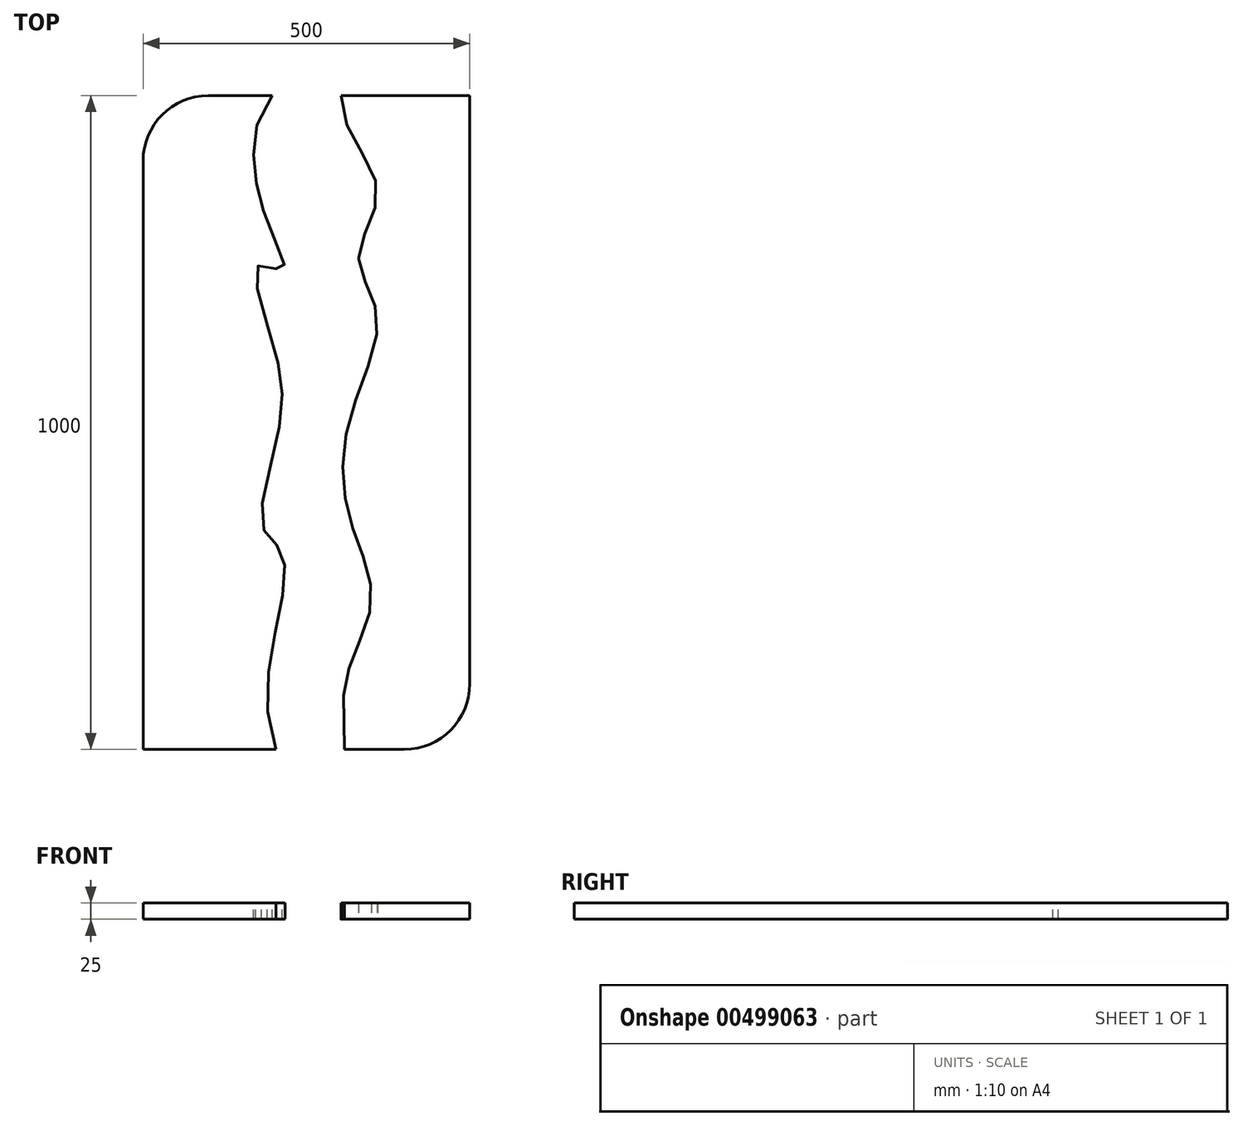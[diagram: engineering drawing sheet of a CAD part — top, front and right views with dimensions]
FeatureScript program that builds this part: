
annotation { "Feature Type Name" : "Feature", "Feature Type Description" : "" }
export const myFeature = defineFeature(function(context is Context, id is Id, definition is map)
    precondition{}
    {
        {
            var Q0;
            Q0=qCreatedBy(makeId("Top.planeOp"),FACE);
            var sketch = newSketch(context, id + "F0", { "sketchPlane" : qUnion([Q0])});
            skLineSegment(sketch, "E0.bottom", {"start": v(-249.04, 423.6) * mm, "end": v(250.96, 423.6) * mm});
            skLineSegment(sketch, "E0.top", {"start": v(-249.04, -576.4) * mm, "end": v(250.96, -576.4) * mm});
            skLineSegment(sketch, "E0.left", {"start": v(-249.04, 423.6) * mm, "end": v(-249.04, -576.4) * mm});
            skLineSegment(sketch, "E0.right", {"start": v(250.96, 423.6) * mm, "end": v(250.96, -576.4) * mm});
            skSolve(sketch);
        }
        {
            var Q0;
            Q0=qSketchRegion(id+"F0",true);
            extrude(context, id + "F1", {"entities" : qUnion([Q0]), "depth" : 25 * mm, "offsetDistance" : 25 * mm});
        }
        {
            var Q0;
            Q0=makeQuery(id+"F1.opExtrude","CAP_FACE",FACE,{"disambiguationData":[OSD([sQuery(id+"F0.wireOp",EDGE,"E0.bottom"),sQuery(id+"F0.wireOp",EDGE,"E0.top"),sQuery(id+"F0.wireOp",EDGE,"E0.left"),sQuery(id+"F0.wireOp",EDGE,"E0.right")])],"isStart":false});
            var sketch = newSketch(context, id + "F2", { "sketchPlane" : qUnion([Q0])});
            skPoint(sketch, "E1.16.internal.snap0", {"position": v(250.96, -76.4) * mm});
            skFitSpline(sketch, "E1", {"points": [v(-51.17, 423.6) * mm, v(-78.61, 314.14) * mm, v(-53, 215.36) * mm, v(-34.71, 156.83) * mm, v(-71.3, 164.14) * mm, v(-51.17, 47.07) * mm, v(-40.2, -82.8) * mm, v(-65.8, -236.47) * mm, v(-36.54, -274.88) * mm, v(-45.69, -391.96) * mm, v(-45.69, -576.4) * mm, v(31.02, -651.88) * mm, v(59.3, -576.4) * mm, v(61.47, -469.15) * mm, v(100.63, -347.33) * mm, v(68, -225.5) * mm, v(65.82, -76.4) * mm, v(109.33, 85.57) * mm, v(81.05, 176.94) * mm, v(109.33, 279.18) * mm, v(54.95, 405.35) * mm, v(54.95, 483.66) * mm, v(-51.17, 423.6) * mm]});
            skSolve(sketch);
        }
        {
            var Q0;
            Q0=qSketchRegion(id+"F2",true);
            extrude(context, id + "F3", {"entities" : qUnion([Q0]), "operationType" : NewBodyOperationType.REMOVE, "oppositeDirection" : true, "depth" : 99 * mm, "offsetDistance" : 25 * mm});
        }
        {
            var Q0;
            Q0=makeQuery(id+"F1.opExtrude","SWEPT_EDGE",EDGE,{"disambiguationData":[OSD([sQuery(id+"F0.wireOp",EDGE,"E0.top"),sQuery(id+"F0.wireOp",EDGE,"E0.right")])]});
            var Q1;
            Q1=makeQuery(id+"F1.opExtrude","SWEPT_EDGE",EDGE,{"disambiguationData":[OSD([sQuery(id+"F0.wireOp",EDGE,"E0.bottom"),sQuery(id+"F0.wireOp",EDGE,"E0.left")])]});
            fillet(context, id + "F4", {"entities" : qUnion([Q0, Q1]), "tangentPropagation" : true, "radius" : 100 * mm, "defaultsChanged" : true, "vertexSettings" : [], "allowEdgeOverflow" : false});
        }
    });
